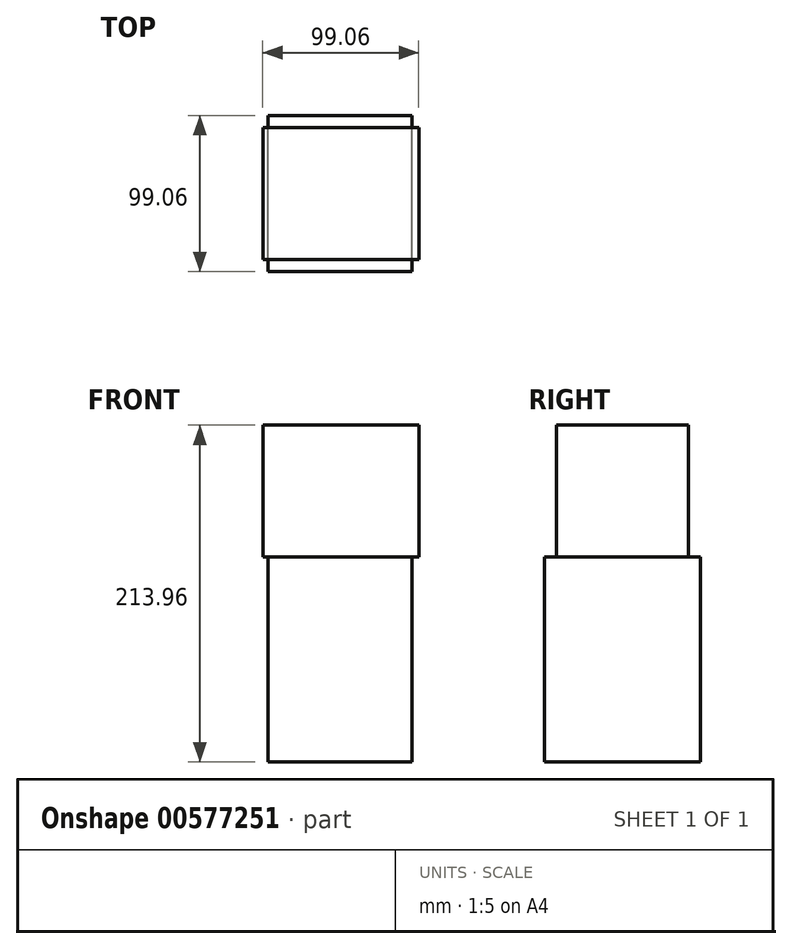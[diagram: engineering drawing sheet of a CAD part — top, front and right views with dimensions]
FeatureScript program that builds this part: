
annotation { "Feature Type Name" : "Feature", "Feature Type Description" : "" }
export const myFeature = defineFeature(function(context is Context, id is Id, definition is map)
    precondition{}
    {
        {
            var Q0;
            Q0=qCreatedBy(makeId("Front.planeOp"),FACE);
            var sketch = newSketch(context, id + "F0", { "sketchPlane" : qUnion([Q0])});
            skLineSegment(sketch, "E0.bottom", {"start": v(45.72, 65.07) * mm, "end": v(-45.72, 65.07) * mm});
            skLineSegment(sketch, "E0.top", {"start": v(45.72, -65.07) * mm, "end": v(-45.72, -65.07) * mm});
            skLineSegment(sketch, "E0.left", {"start": v(45.72, 65.07) * mm, "end": v(45.72, -65.07) * mm});
            skLineSegment(sketch, "E0.right", {"start": v(-45.72, 65.07) * mm, "end": v(-45.72, -65.07) * mm});
            skPoint(sketch, "E0.middle", {"position": v(0, 0) * mm});
            skLineSegment(sketch, "E1.bottom", {"start": v(-49.15, 65.07) * mm, "end": v(49.91, 65.07) * mm});
            skLineSegment(sketch, "E1.top", {"start": v(-49.15, 148.9) * mm, "end": v(49.91, 148.9) * mm});
            skLineSegment(sketch, "E1.left", {"start": v(-49.15, 65.07) * mm, "end": v(-49.15, 148.9) * mm});
            skLineSegment(sketch, "E1.right", {"start": v(49.91, 65.07) * mm, "end": v(49.91, 148.9) * mm});
            skSolve(sketch);
        }
        {
            var Q0;
            Q0=makeQuery(id+"F0.imprint","IMPRINT",FACE,{"disambiguationData":[TD([[makeQuery(id+"F0.imprint","IMPRINT",EDGE,{"derivedFrom":sQuery(id+"F0.wireOp",EDGE,"E1.top")}),-1.0]])]});
            extrude(context, id + "F1", {"entities" : qUnion([Q0]), "endBound" : BoundingType.SYMMETRIC, "depth" : 83.82 * mm, "offsetDistance" : 25.4 * mm});
        }
        {
            var Q0;
            Q0=makeQuery(id+"F0.imprint","IMPRINT",FACE,{"disambiguationData":[TD([[makeQuery(id+"F0.imprint","IMPRINT",EDGE,{"derivedFrom":sQuery(id+"F0.wireOp",EDGE,"E0.top")}),-1.0]])]});
            extrude(context, id + "F2", {"entities" : qUnion([Q0]), "operationType" : NewBodyOperationType.ADD, "endBound" : BoundingType.SYMMETRIC, "depth" : 99.06 * mm, "offsetDistance" : 25.4 * mm});
        }
    });
